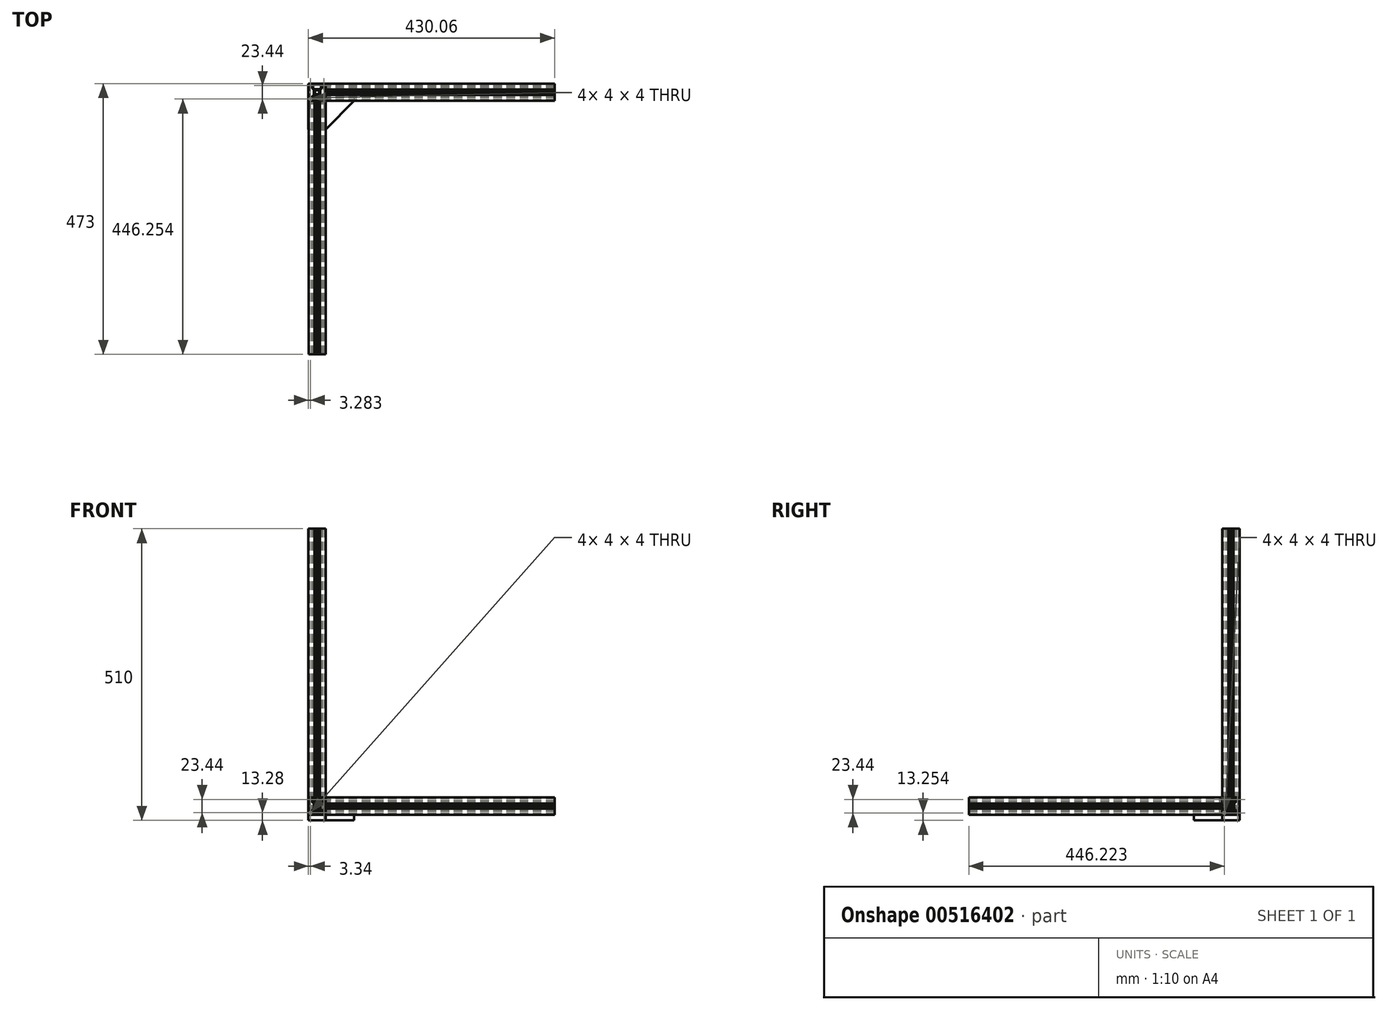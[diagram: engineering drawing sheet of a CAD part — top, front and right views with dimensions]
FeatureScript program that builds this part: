
annotation { "Feature Type Name" : "Feature", "Feature Type Description" : "" }
export const myFeature = defineFeature(function(context is Context, id is Id, definition is map)
    precondition{}
    {
        {
            var Q0;
            Q0=qCreatedBy(makeId("Front.planeOp"),FACE);
            var sketch = newSketch(context, id + "F0", { "sketchPlane" : qUnion([Q0])});
            skLineSegment(sketch, "E0", {"start": v(-15, 15) * mm, "end": v(-4.6, 15) * mm});
            skLineSegment(sketch, "E1", {"start": v(-4.6, 15) * mm, "end": v(-4.6, 14.5) * mm});
            skLineSegment(sketch, "E2", {"start": v(-4.6, 14.5) * mm, "end": v(-4.1, 14.5) * mm});
            skLineSegment(sketch, "E3", {"start": v(-4.1, 14.5) * mm, "end": v(-4.1, 12.8) * mm});
            skLineSegment(sketch, "E4", {"start": v(-4.1, 12.8) * mm, "end": v(-8.4, 12.8) * mm});
            skLineSegment(sketch, "E5", {"start": v(-8.4, 12.8) * mm, "end": v(-8.4, 9.8) * mm});
            skLineSegment(sketch, "E6", {"start": v(-8.4, 9.8) * mm, "end": v(-4.35, 5.75) * mm});
            skLineSegment(sketch, "E7", {"start": v(-4.35, 5.75) * mm, "end": v(-0.5, 5.75) * mm});
            skLineSegment(sketch, "E8", {"start": v(-0.5, 5.75) * mm, "end": v(0, 5.25) * mm});
            skLineSegment(sketch, "E9", {"start": v(0, 5.25) * mm, "end": v(0.5, 5.75) * mm});
            skLineSegment(sketch, "E10", {"start": v(0.5, 5.75) * mm, "end": v(4.35, 5.75) * mm});
            skLineSegment(sketch, "E11", {"start": v(4.35, 5.75) * mm, "end": v(8.4, 9.8) * mm});
            skLineSegment(sketch, "E12", {"start": v(8.4, 9.8) * mm, "end": v(8.4, 12.8) * mm});
            skLineSegment(sketch, "E13", {"start": v(8.4, 12.8) * mm, "end": v(4.6, 12.8) * mm});
            skLineSegment(sketch, "E14", {"start": v(4.6, 12.8) * mm, "end": v(4.6, 14.5) * mm});
            skLineSegment(sketch, "E15", {"start": v(4.6, 14.5) * mm, "end": v(5.1, 14.5) * mm});
            skLineSegment(sketch, "E16", {"start": v(5.1, 14.5) * mm, "end": v(5.1, 15) * mm});
            skLineSegment(sketch, "E17", {"start": v(5.1, 15) * mm, "end": v(15, 15) * mm});
            skLineSegment(sketch, "E18", {"start": v(15, 15) * mm, "end": v(15, 4.6) * mm});
            skLineSegment(sketch, "E19", {"start": v(15, 4.6) * mm, "end": v(14.5, 4.6) * mm});
            skLineSegment(sketch, "E20", {"start": v(14.5, 4.6) * mm, "end": v(14.5, 4.1) * mm});
            skLineSegment(sketch, "E21", {"start": v(14.5, 4.1) * mm, "end": v(12.8, 4.1) * mm});
            skLineSegment(sketch, "E22", {"start": v(12.8, 4.1) * mm, "end": v(12.8, 8.4) * mm});
            skLineSegment(sketch, "E23", {"start": v(12.8, 8.4) * mm, "end": v(9.8, 8.4) * mm});
            skLineSegment(sketch, "E24", {"start": v(9.8, 8.4) * mm, "end": v(5.75, 4.35) * mm});
            skLineSegment(sketch, "E25", {"start": v(5.75, 4.35) * mm, "end": v(5.75, 0.5) * mm});
            skLineSegment(sketch, "E26", {"start": v(5.25, 0) * mm, "end": v(5.75, 0.5) * mm});
            skLineSegment(sketch, "E27", {"start": v(5.75, -0.5) * mm, "end": v(5.25, 0) * mm});
            skLineSegment(sketch, "E28", {"start": v(5.75, -0.5) * mm, "end": v(5.75, -4.35) * mm});
            skLineSegment(sketch, "E29", {"start": v(5.75, -4.35) * mm, "end": v(9.8, -8.4) * mm});
            skLineSegment(sketch, "E30", {"start": v(9.8, -8.4) * mm, "end": v(12.8, -8.4) * mm});
            skLineSegment(sketch, "E31", {"start": v(12.8, -8.4) * mm, "end": v(12.8, -3.79) * mm});
            skLineSegment(sketch, "E32", {"start": v(12.8, -3.79) * mm, "end": v(14.5, -3.79) * mm});
            skLineSegment(sketch, "E33", {"start": v(14.5, -3.79) * mm, "end": v(14.5, -4.29) * mm});
            skLineSegment(sketch, "E34", {"start": v(14.5, -4.29) * mm, "end": v(15, -4.29) * mm});
            skLineSegment(sketch, "E35", {"start": v(15, -4.29) * mm, "end": v(15, -15) * mm});
            skLineSegment(sketch, "E36", {"start": v(15, -15) * mm, "end": v(5.1, -15) * mm});
            skLineSegment(sketch, "E37", {"start": v(5.1, -15) * mm, "end": v(5.1, -14.5) * mm});
            skLineSegment(sketch, "E38", {"start": v(5.1, -14.5) * mm, "end": v(4.6, -14.5) * mm});
            skLineSegment(sketch, "E39", {"start": v(4.6, -14.5) * mm, "end": v(4.6, -12.8) * mm});
            skLineSegment(sketch, "E40", {"start": v(4.6, -12.8) * mm, "end": v(8.4, -12.8) * mm});
            skLineSegment(sketch, "E41", {"start": v(8.4, -12.8) * mm, "end": v(8.4, -9.8) * mm});
            skLineSegment(sketch, "E42", {"start": v(8.4, -9.8) * mm, "end": v(4.35, -5.75) * mm});
            skLineSegment(sketch, "E43", {"start": v(4.35, -5.75) * mm, "end": v(0.5, -5.75) * mm});
            skLineSegment(sketch, "E44", {"start": v(0.5, -5.75) * mm, "end": v(0, -5.25) * mm});
            skLineSegment(sketch, "E45", {"start": v(0, -5.25) * mm, "end": v(-0.5, -5.75) * mm});
            skLineSegment(sketch, "E46", {"start": v(-0.5, -5.75) * mm, "end": v(-4.35, -5.75) * mm});
            skLineSegment(sketch, "E47", {"start": v(-4.35, -5.75) * mm, "end": v(-8.4, -9.8) * mm});
            skLineSegment(sketch, "E48", {"start": v(-8.4, -9.8) * mm, "end": v(-8.4, -12.8) * mm});
            skLineSegment(sketch, "E49", {"start": v(-8.4, -12.8) * mm, "end": v(-4.09, -12.8) * mm});
            skLineSegment(sketch, "E50", {"start": v(-4.09, -12.8) * mm, "end": v(-4.09, -14.5) * mm});
            skLineSegment(sketch, "E51", {"start": v(-4.09, -14.5) * mm, "end": v(-4.6, -14.5) * mm});
            skLineSegment(sketch, "E52", {"start": v(-4.6, -14.5) * mm, "end": v(-4.6, -15) * mm});
            skLineSegment(sketch, "E53", {"start": v(-4.6, -15) * mm, "end": v(-15, -15) * mm});
            skLineSegment(sketch, "E54", {"start": v(-15, -15) * mm, "end": v(-15, -4.29) * mm});
            skLineSegment(sketch, "E55", {"start": v(-15, -4.29) * mm, "end": v(-14.5, -4.29) * mm});
            skLineSegment(sketch, "E56", {"start": v(-14.5, -4.29) * mm, "end": v(-14.5, -4.1) * mm});
            skLineSegment(sketch, "E57", {"start": v(-14.5, -4.1) * mm, "end": v(-12.8, -4.1) * mm});
            skLineSegment(sketch, "E58", {"start": v(-12.8, -4.1) * mm, "end": v(-12.8, -8.4) * mm});
            skLineSegment(sketch, "E59", {"start": v(-12.8, -8.4) * mm, "end": v(-9.8, -8.4) * mm});
            skLineSegment(sketch, "E60", {"start": v(-9.8, -8.4) * mm, "end": v(-5.75, -4.35) * mm});
            skLineSegment(sketch, "E61", {"start": v(-5.75, -4.35) * mm, "end": v(-5.75, -0.5) * mm});
            skLineSegment(sketch, "E62", {"start": v(-5.75, -0.5) * mm, "end": v(-5.25, 0) * mm});
            skLineSegment(sketch, "E63", {"start": v(-5.25, 0) * mm, "end": v(-5.75, 0.5) * mm});
            skLineSegment(sketch, "E64", {"start": v(-5.75, 0.5) * mm, "end": v(-5.75, 4.35) * mm});
            skLineSegment(sketch, "E65", {"start": v(-5.75, 4.35) * mm, "end": v(-9.8, 8.4) * mm});
            skLineSegment(sketch, "E66", {"start": v(-9.8, 8.4) * mm, "end": v(-12.8, 8.4) * mm});
            skLineSegment(sketch, "E67", {"start": v(-12.8, 8.4) * mm, "end": v(-12.8, 4.1) * mm});
            skLineSegment(sketch, "E68", {"start": v(-12.8, 4.1) * mm, "end": v(-14.5, 4.1) * mm});
            skLineSegment(sketch, "E69", {"start": v(-14.5, 4.1) * mm, "end": v(-14.5, 4.6) * mm});
            skLineSegment(sketch, "E70", {"start": v(-14.5, 4.6) * mm, "end": v(-15, 4.6) * mm});
            skLineSegment(sketch, "E71", {"start": v(-15, 4.6) * mm, "end": v(-15, 15) * mm});
            skSolve(sketch);
        }
        {
            var Q0;
            Q0=qCreatedBy(makeId("Front.planeOp"),FACE);
            var sketch = newSketch(context, id + "F1", { "sketchPlane" : qUnion([Q0])});
            skCircle(sketch, "E72", {"center": v(0, 0) * mm, "radius": 3.7 * mm});
            skLineSegment(sketch, "E73.bottom", {"start": v(9.72, 13.72) * mm, "end": v(13.72, 13.72) * mm});
            skLineSegment(sketch, "E73.top", {"start": v(9.72, 9.72) * mm, "end": v(13.72, 9.72) * mm});
            skLineSegment(sketch, "E73.left", {"start": v(9.72, 13.72) * mm, "end": v(9.72, 9.72) * mm});
            skLineSegment(sketch, "E73.right", {"start": v(13.72, 13.72) * mm, "end": v(13.72, 9.72) * mm});
            skLineSegment(sketch, "E74.bottom", {"start": v(9.72, -9.72) * mm, "end": v(13.72, -9.72) * mm});
            skLineSegment(sketch, "E74.top", {"start": v(9.72, -13.72) * mm, "end": v(13.72, -13.72) * mm});
            skLineSegment(sketch, "E74.left", {"start": v(9.72, -9.72) * mm, "end": v(9.72, -13.72) * mm});
            skLineSegment(sketch, "E74.right", {"start": v(13.72, -9.72) * mm, "end": v(13.72, -13.72) * mm});
            skLineSegment(sketch, "E75.bottom", {"start": v(-13.72, -9.72) * mm, "end": v(-9.72, -9.72) * mm});
            skLineSegment(sketch, "E75.top", {"start": v(-13.72, -13.72) * mm, "end": v(-9.72, -13.72) * mm});
            skLineSegment(sketch, "E75.left", {"start": v(-13.72, -9.72) * mm, "end": v(-13.72, -13.72) * mm});
            skLineSegment(sketch, "E75.right", {"start": v(-9.72, -9.72) * mm, "end": v(-9.72, -13.72) * mm});
            skLineSegment(sketch, "E76.bottom", {"start": v(-13.72, 13.72) * mm, "end": v(-9.72, 13.72) * mm});
            skLineSegment(sketch, "E76.top", {"start": v(-13.72, 9.72) * mm, "end": v(-9.72, 9.72) * mm});
            skLineSegment(sketch, "E76.left", {"start": v(-13.72, 13.72) * mm, "end": v(-13.72, 9.72) * mm});
            skLineSegment(sketch, "E76.right", {"start": v(-9.72, 13.72) * mm, "end": v(-9.72, 9.72) * mm});
            skSolve(sketch);
        }
        {
            var Q0;
            Q0=qSketchRegion(id+"F0",true);
            extrude(context, id + "F2", {"entities" : qUnion([Q0]), "depth" : 443 * mm, "offsetDistance" : 25 * mm});
        }
        {
            var Q0;
            Q0=qSketchRegion(id+"F1",true);
            extrude(context, id + "F3", {"entities" : qUnion([Q0]), "operationType" : NewBodyOperationType.REMOVE, "endBound" : BoundingType.THROUGH_ALL, "depth" : 25 * mm, "offsetDistance" : 25 * mm});
        }
        {
            var Q0;
            Q0=qCreatedBy(makeId("Top.planeOp"),FACE);
            cPlane(context, id + "F4", {"entities" : qUnion([Q0]), "cplaneType" : CPlaneType.OFFSET, "offset" : 15 * mm, "width" : 150 * mm, "height" : 150 * mm});
        }
        {
            var Q0;
            Q0=qCreatedBy(id+"F4.planeOp",FACE);
            var sketch = newSketch(context, id + "F5", { "sketchPlane" : qUnion([Q0])});
            skLineSegment(sketch, "E77", {"start": v(-15.06, 14.97) * mm, "end": v(-4.66, 14.97) * mm});
            skLineSegment(sketch, "E78", {"start": v(-4.66, 14.97) * mm, "end": v(-4.66, 14.47) * mm});
            skLineSegment(sketch, "E79", {"start": v(-4.66, 14.47) * mm, "end": v(-4.16, 14.47) * mm});
            skLineSegment(sketch, "E80", {"start": v(-4.16, 14.47) * mm, "end": v(-4.16, 12.77) * mm});
            skLineSegment(sketch, "E81", {"start": v(-4.16, 12.77) * mm, "end": v(-8.46, 12.77) * mm});
            skLineSegment(sketch, "E82", {"start": v(-8.46, 12.77) * mm, "end": v(-8.46, 9.77) * mm});
            skLineSegment(sketch, "E83", {"start": v(-8.46, 9.77) * mm, "end": v(-4.4, 5.72) * mm});
            skLineSegment(sketch, "E84", {"start": v(-4.4, 5.72) * mm, "end": v(-0.56, 5.72) * mm});
            skLineSegment(sketch, "E85", {"start": v(-0.56, 5.72) * mm, "end": v(-0.06, 5.22) * mm});
            skLineSegment(sketch, "E86", {"start": v(-0.06, 5.22) * mm, "end": v(0.44, 5.72) * mm});
            skLineSegment(sketch, "E87", {"start": v(0.44, 5.72) * mm, "end": v(4.3, 5.72) * mm});
            skLineSegment(sketch, "E88", {"start": v(4.3, 5.72) * mm, "end": v(8.34, 9.77) * mm});
            skLineSegment(sketch, "E89", {"start": v(8.34, 9.77) * mm, "end": v(8.34, 12.77) * mm});
            skLineSegment(sketch, "E90", {"start": v(8.34, 12.77) * mm, "end": v(4.55, 12.77) * mm});
            skLineSegment(sketch, "E91", {"start": v(4.55, 12.77) * mm, "end": v(4.55, 14.47) * mm});
            skLineSegment(sketch, "E92", {"start": v(4.55, 14.47) * mm, "end": v(5.05, 14.47) * mm});
            skLineSegment(sketch, "E93", {"start": v(5.05, 14.47) * mm, "end": v(5.05, 14.97) * mm});
            skLineSegment(sketch, "E94", {"start": v(5.05, 14.97) * mm, "end": v(14.94, 14.97) * mm});
            skLineSegment(sketch, "E95", {"start": v(14.94, 14.97) * mm, "end": v(14.94, 4.57) * mm});
            skLineSegment(sketch, "E96", {"start": v(14.94, 4.57) * mm, "end": v(14.44, 4.57) * mm});
            skLineSegment(sketch, "E97", {"start": v(14.44, 4.57) * mm, "end": v(14.44, 4.07) * mm});
            skLineSegment(sketch, "E98", {"start": v(14.44, 4.07) * mm, "end": v(12.74, 4.07) * mm});
            skLineSegment(sketch, "E99", {"start": v(12.74, 4.07) * mm, "end": v(12.74, 8.37) * mm});
            skLineSegment(sketch, "E100", {"start": v(12.74, 8.37) * mm, "end": v(9.74, 8.37) * mm});
            skLineSegment(sketch, "E101", {"start": v(9.74, 8.37) * mm, "end": v(5.7, 4.32) * mm});
            skLineSegment(sketch, "E102", {"start": v(5.7, 4.32) * mm, "end": v(5.7, 0.47) * mm});
            skLineSegment(sketch, "E103", {"start": v(5.2, -0.03) * mm, "end": v(5.7, 0.47) * mm});
            skLineSegment(sketch, "E104", {"start": v(5.7, -0.53) * mm, "end": v(5.2, -0.03) * mm});
            skLineSegment(sketch, "E105", {"start": v(5.7, -0.53) * mm, "end": v(5.7, -4.38) * mm});
            skLineSegment(sketch, "E106", {"start": v(5.7, -4.38) * mm, "end": v(9.74, -8.43) * mm});
            skLineSegment(sketch, "E107", {"start": v(9.74, -8.43) * mm, "end": v(12.74, -8.43) * mm});
            skLineSegment(sketch, "E108", {"start": v(12.74, -8.43) * mm, "end": v(12.74, -3.81) * mm});
            skLineSegment(sketch, "E109", {"start": v(12.74, -3.81) * mm, "end": v(14.44, -3.81) * mm});
            skLineSegment(sketch, "E110", {"start": v(14.44, -3.81) * mm, "end": v(14.44, -4.31) * mm});
            skLineSegment(sketch, "E111", {"start": v(14.44, -4.31) * mm, "end": v(14.94, -4.31) * mm});
            skLineSegment(sketch, "E112", {"start": v(14.94, -4.31) * mm, "end": v(14.94, -15.03) * mm});
            skLineSegment(sketch, "E113", {"start": v(14.94, -15.03) * mm, "end": v(5.05, -15.03) * mm});
            skLineSegment(sketch, "E114", {"start": v(5.05, -15.03) * mm, "end": v(5.05, -14.53) * mm});
            skLineSegment(sketch, "E115", {"start": v(5.05, -14.53) * mm, "end": v(4.55, -14.53) * mm});
            skLineSegment(sketch, "E116", {"start": v(4.55, -14.53) * mm, "end": v(4.55, -12.83) * mm});
            skLineSegment(sketch, "E117", {"start": v(4.55, -12.83) * mm, "end": v(8.34, -12.83) * mm});
            skLineSegment(sketch, "E118", {"start": v(8.34, -12.83) * mm, "end": v(8.34, -9.83) * mm});
            skLineSegment(sketch, "E119", {"start": v(8.34, -9.83) * mm, "end": v(4.3, -5.78) * mm});
            skLineSegment(sketch, "E120", {"start": v(4.3, -5.78) * mm, "end": v(0.44, -5.78) * mm});
            skLineSegment(sketch, "E121", {"start": v(0.44, -5.78) * mm, "end": v(-0.06, -5.28) * mm});
            skLineSegment(sketch, "E122", {"start": v(-0.06, -5.28) * mm, "end": v(-0.56, -5.78) * mm});
            skLineSegment(sketch, "E123", {"start": v(-0.56, -5.78) * mm, "end": v(-4.4, -5.78) * mm});
            skLineSegment(sketch, "E124", {"start": v(-4.4, -5.78) * mm, "end": v(-8.46, -9.83) * mm});
            skLineSegment(sketch, "E125", {"start": v(-8.46, -9.83) * mm, "end": v(-8.46, -12.83) * mm});
            skLineSegment(sketch, "E126", {"start": v(-8.46, -12.83) * mm, "end": v(-4.14, -12.83) * mm});
            skLineSegment(sketch, "E127", {"start": v(-4.14, -12.83) * mm, "end": v(-4.14, -14.53) * mm});
            skLineSegment(sketch, "E128", {"start": v(-4.14, -14.53) * mm, "end": v(-4.66, -14.53) * mm});
            skLineSegment(sketch, "E129", {"start": v(-4.66, -14.53) * mm, "end": v(-4.66, -15.03) * mm});
            skLineSegment(sketch, "E130", {"start": v(-4.66, -15.03) * mm, "end": v(-15.06, -15.03) * mm});
            skLineSegment(sketch, "E131", {"start": v(-15.06, -15.03) * mm, "end": v(-15.06, -4.31) * mm});
            skLineSegment(sketch, "E132", {"start": v(-15.06, -4.31) * mm, "end": v(-14.56, -4.31) * mm});
            skLineSegment(sketch, "E133", {"start": v(-14.56, -4.31) * mm, "end": v(-14.56, -4.13) * mm});
            skLineSegment(sketch, "E134", {"start": v(-14.56, -4.13) * mm, "end": v(-12.86, -4.13) * mm});
            skLineSegment(sketch, "E135", {"start": v(-12.86, -4.13) * mm, "end": v(-12.86, -8.43) * mm});
            skLineSegment(sketch, "E136", {"start": v(-12.86, -8.43) * mm, "end": v(-9.86, -8.43) * mm});
            skLineSegment(sketch, "E137", {"start": v(-9.86, -8.43) * mm, "end": v(-5.8, -4.38) * mm});
            skLineSegment(sketch, "E138", {"start": v(-5.8, -4.38) * mm, "end": v(-5.8, -0.53) * mm});
            skLineSegment(sketch, "E139", {"start": v(-5.8, -0.53) * mm, "end": v(-5.3, -0.03) * mm});
            skLineSegment(sketch, "E140", {"start": v(-5.3, -0.03) * mm, "end": v(-5.8, 0.47) * mm});
            skLineSegment(sketch, "E141", {"start": v(-5.8, 0.47) * mm, "end": v(-5.8, 4.32) * mm});
            skLineSegment(sketch, "E142", {"start": v(-5.8, 4.32) * mm, "end": v(-9.86, 8.37) * mm});
            skLineSegment(sketch, "E143", {"start": v(-9.86, 8.37) * mm, "end": v(-12.86, 8.37) * mm});
            skLineSegment(sketch, "E144", {"start": v(-12.86, 8.37) * mm, "end": v(-12.86, 4.07) * mm});
            skLineSegment(sketch, "E145", {"start": v(-12.86, 4.07) * mm, "end": v(-14.56, 4.07) * mm});
            skLineSegment(sketch, "E146", {"start": v(-14.56, 4.07) * mm, "end": v(-14.56, 4.57) * mm});
            skLineSegment(sketch, "E147", {"start": v(-14.56, 4.57) * mm, "end": v(-15.06, 4.57) * mm});
            skLineSegment(sketch, "E148", {"start": v(-15.06, 4.57) * mm, "end": v(-15.06, 14.97) * mm});
            skSolve(sketch);
        }
        {
            var Q0;
            Q0=qCreatedBy(id+"F4.planeOp",FACE);
            var sketch = newSketch(context, id + "F6", { "sketchPlane" : qUnion([Q0])});
            skCircle(sketch, "E149", {"center": v(0, 0) * mm, "radius": 3.7 * mm});
            skLineSegment(sketch, "E150.bottom", {"start": v(9.66, 13.69) * mm, "end": v(13.66, 13.69) * mm});
            skLineSegment(sketch, "E150.top", {"start": v(9.66, 9.69) * mm, "end": v(13.66, 9.69) * mm});
            skLineSegment(sketch, "E150.left", {"start": v(9.66, 13.69) * mm, "end": v(9.66, 9.69) * mm});
            skLineSegment(sketch, "E150.right", {"start": v(13.66, 13.69) * mm, "end": v(13.66, 9.69) * mm});
            skLineSegment(sketch, "E151.bottom", {"start": v(9.66, -9.75) * mm, "end": v(13.66, -9.75) * mm});
            skLineSegment(sketch, "E151.top", {"start": v(9.66, -13.75) * mm, "end": v(13.66, -13.75) * mm});
            skLineSegment(sketch, "E151.left", {"start": v(9.66, -9.75) * mm, "end": v(9.66, -13.75) * mm});
            skLineSegment(sketch, "E151.right", {"start": v(13.66, -9.75) * mm, "end": v(13.66, -13.75) * mm});
            skLineSegment(sketch, "E152.bottom", {"start": v(-13.78, -9.75) * mm, "end": v(-9.78, -9.75) * mm});
            skLineSegment(sketch, "E152.top", {"start": v(-13.78, -13.75) * mm, "end": v(-9.78, -13.75) * mm});
            skLineSegment(sketch, "E152.left", {"start": v(-13.78, -9.75) * mm, "end": v(-13.78, -13.75) * mm});
            skLineSegment(sketch, "E152.right", {"start": v(-9.78, -9.75) * mm, "end": v(-9.78, -13.75) * mm});
            skLineSegment(sketch, "E153.bottom", {"start": v(-13.78, 13.7) * mm, "end": v(-9.78, 13.7) * mm});
            skLineSegment(sketch, "E153.top", {"start": v(-13.78, 9.7) * mm, "end": v(-9.78, 9.7) * mm});
            skLineSegment(sketch, "E153.left", {"start": v(-13.78, 13.7) * mm, "end": v(-13.78, 9.7) * mm});
            skLineSegment(sketch, "E153.right", {"start": v(-9.78, 13.7) * mm, "end": v(-9.78, 9.7) * mm});
            skSolve(sketch);
        }
        {
            var Q0;
            Q0 = qSketchRegion(id + "F5", true);
            extrude(context, id + "F7", {"entities" : qUnion([Q0]), "depth" : 500 * mm, "offsetDistance" : 25 * mm});
        }
        {
            var Q0;
            Q0 = qSketchRegion(id + "F6", true);
            extrude(context, id + "F8", {"entities" : qUnion([Q0]), "operationType" : NewBodyOperationType.REMOVE, "endBound" : BoundingType.THROUGH_ALL, "depth" : 25 * mm, "offsetDistance" : 25 * mm});
        }
        {
            var Q0;
            Q0=makeQuery(id+"F7.opExtrude","SWEPT_BODY",BODY,{"disambiguationData":[OSD([sQuery(id+"F5.wireOp",EDGE,"E77"),sQuery(id+"F5.wireOp",EDGE,"E78"),sQuery(id+"F5.wireOp",EDGE,"E79"),sQuery(id+"F5.wireOp",EDGE,"E80"),sQuery(id+"F5.wireOp",EDGE,"E81"),sQuery(id+"F5.wireOp",EDGE,"E82"),sQuery(id+"F5.wireOp",EDGE,"E83"),sQuery(id+"F5.wireOp",EDGE,"E84"),sQuery(id+"F5.wireOp",EDGE,"E85"),sQuery(id+"F5.wireOp",EDGE,"E86"),sQuery(id+"F5.wireOp",EDGE,"E87"),sQuery(id+"F5.wireOp",EDGE,"E88"),sQuery(id+"F5.wireOp",EDGE,"E89"),sQuery(id+"F5.wireOp",EDGE,"E90"),sQuery(id+"F5.wireOp",EDGE,"E91"),sQuery(id+"F5.wireOp",EDGE,"E92"),sQuery(id+"F5.wireOp",EDGE,"E93"),sQuery(id+"F5.wireOp",EDGE,"E94"),sQuery(id+"F5.wireOp",EDGE,"E95"),sQuery(id+"F5.wireOp",EDGE,"E96"),sQuery(id+"F5.wireOp",EDGE,"E97"),sQuery(id+"F5.wireOp",EDGE,"E98"),sQuery(id+"F5.wireOp",EDGE,"E99"),sQuery(id+"F5.wireOp",EDGE,"E100"),sQuery(id+"F5.wireOp",EDGE,"E101"),sQuery(id+"F5.wireOp",EDGE,"E102"),sQuery(id+"F5.wireOp",EDGE,"E103"),sQuery(id+"F5.wireOp",EDGE,"E104"),sQuery(id+"F5.wireOp",EDGE,"E105"),sQuery(id+"F5.wireOp",EDGE,"E106"),sQuery(id+"F5.wireOp",EDGE,"E107"),sQuery(id+"F5.wireOp",EDGE,"E108"),sQuery(id+"F5.wireOp",EDGE,"E109"),sQuery(id+"F5.wireOp",EDGE,"E110"),sQuery(id+"F5.wireOp",EDGE,"E111"),sQuery(id+"F5.wireOp",EDGE,"E112"),sQuery(id+"F5.wireOp",EDGE,"E113"),sQuery(id+"F5.wireOp",EDGE,"E114"),sQuery(id+"F5.wireOp",EDGE,"E115"),sQuery(id+"F5.wireOp",EDGE,"E116"),sQuery(id+"F5.wireOp",EDGE,"E117"),sQuery(id+"F5.wireOp",EDGE,"E118"),sQuery(id+"F5.wireOp",EDGE,"E119"),sQuery(id+"F5.wireOp",EDGE,"E120"),sQuery(id+"F5.wireOp",EDGE,"E121"),sQuery(id+"F5.wireOp",EDGE,"E122"),sQuery(id+"F5.wireOp",EDGE,"E123"),sQuery(id+"F5.wireOp",EDGE,"E124"),sQuery(id+"F5.wireOp",EDGE,"E125"),sQuery(id+"F5.wireOp",EDGE,"E126"),sQuery(id+"F5.wireOp",EDGE,"E127"),sQuery(id+"F5.wireOp",EDGE,"E128"),sQuery(id+"F5.wireOp",EDGE,"E129"),sQuery(id+"F5.wireOp",EDGE,"E130"),sQuery(id+"F5.wireOp",EDGE,"E131"),sQuery(id+"F5.wireOp",EDGE,"E132"),sQuery(id+"F5.wireOp",EDGE,"E133"),sQuery(id+"F5.wireOp",EDGE,"E134"),sQuery(id+"F5.wireOp",EDGE,"E135"),sQuery(id+"F5.wireOp",EDGE,"E136"),sQuery(id+"F5.wireOp",EDGE,"E137"),sQuery(id+"F5.wireOp",EDGE,"E138"),sQuery(id+"F5.wireOp",EDGE,"E139"),sQuery(id+"F5.wireOp",EDGE,"E140"),sQuery(id+"F5.wireOp",EDGE,"E141"),sQuery(id+"F5.wireOp",EDGE,"E142"),sQuery(id+"F5.wireOp",EDGE,"E143"),sQuery(id+"F5.wireOp",EDGE,"E144"),sQuery(id+"F5.wireOp",EDGE,"E145"),sQuery(id+"F5.wireOp",EDGE,"E146"),sQuery(id+"F5.wireOp",EDGE,"E147"),sQuery(id+"F5.wireOp",EDGE,"E148")])]});
            transform(context, id + "F9", {"entities" : qUnion([Q0]), "transformType" : TransformType.TRANSLATION_3D, "dx" : 0 * mm, "dy" : 15 * mm, "dz" : 0 * mm, "makeCopy" : false});
        }
        {
            var Q0;
            Q0=makeQuery(id+"F7.opExtrude","SWEPT_BODY",BODY,{"disambiguationData":[OSD([sQuery(id+"F5.wireOp",EDGE,"E77"),sQuery(id+"F5.wireOp",EDGE,"E78"),sQuery(id+"F5.wireOp",EDGE,"E79"),sQuery(id+"F5.wireOp",EDGE,"E80"),sQuery(id+"F5.wireOp",EDGE,"E81"),sQuery(id+"F5.wireOp",EDGE,"E82"),sQuery(id+"F5.wireOp",EDGE,"E83"),sQuery(id+"F5.wireOp",EDGE,"E84"),sQuery(id+"F5.wireOp",EDGE,"E85"),sQuery(id+"F5.wireOp",EDGE,"E86"),sQuery(id+"F5.wireOp",EDGE,"E87"),sQuery(id+"F5.wireOp",EDGE,"E88"),sQuery(id+"F5.wireOp",EDGE,"E89"),sQuery(id+"F5.wireOp",EDGE,"E90"),sQuery(id+"F5.wireOp",EDGE,"E91"),sQuery(id+"F5.wireOp",EDGE,"E92"),sQuery(id+"F5.wireOp",EDGE,"E93"),sQuery(id+"F5.wireOp",EDGE,"E94"),sQuery(id+"F5.wireOp",EDGE,"E95"),sQuery(id+"F5.wireOp",EDGE,"E96"),sQuery(id+"F5.wireOp",EDGE,"E97"),sQuery(id+"F5.wireOp",EDGE,"E98"),sQuery(id+"F5.wireOp",EDGE,"E99"),sQuery(id+"F5.wireOp",EDGE,"E100"),sQuery(id+"F5.wireOp",EDGE,"E101"),sQuery(id+"F5.wireOp",EDGE,"E102"),sQuery(id+"F5.wireOp",EDGE,"E103"),sQuery(id+"F5.wireOp",EDGE,"E104"),sQuery(id+"F5.wireOp",EDGE,"E105"),sQuery(id+"F5.wireOp",EDGE,"E106"),sQuery(id+"F5.wireOp",EDGE,"E107"),sQuery(id+"F5.wireOp",EDGE,"E108"),sQuery(id+"F5.wireOp",EDGE,"E109"),sQuery(id+"F5.wireOp",EDGE,"E110"),sQuery(id+"F5.wireOp",EDGE,"E111"),sQuery(id+"F5.wireOp",EDGE,"E112"),sQuery(id+"F5.wireOp",EDGE,"E113"),sQuery(id+"F5.wireOp",EDGE,"E114"),sQuery(id+"F5.wireOp",EDGE,"E115"),sQuery(id+"F5.wireOp",EDGE,"E116"),sQuery(id+"F5.wireOp",EDGE,"E117"),sQuery(id+"F5.wireOp",EDGE,"E118"),sQuery(id+"F5.wireOp",EDGE,"E119"),sQuery(id+"F5.wireOp",EDGE,"E120"),sQuery(id+"F5.wireOp",EDGE,"E121"),sQuery(id+"F5.wireOp",EDGE,"E122"),sQuery(id+"F5.wireOp",EDGE,"E123"),sQuery(id+"F5.wireOp",EDGE,"E124"),sQuery(id+"F5.wireOp",EDGE,"E125"),sQuery(id+"F5.wireOp",EDGE,"E126"),sQuery(id+"F5.wireOp",EDGE,"E127"),sQuery(id+"F5.wireOp",EDGE,"E128"),sQuery(id+"F5.wireOp",EDGE,"E129"),sQuery(id+"F5.wireOp",EDGE,"E130"),sQuery(id+"F5.wireOp",EDGE,"E131"),sQuery(id+"F5.wireOp",EDGE,"E132"),sQuery(id+"F5.wireOp",EDGE,"E133"),sQuery(id+"F5.wireOp",EDGE,"E134"),sQuery(id+"F5.wireOp",EDGE,"E135"),sQuery(id+"F5.wireOp",EDGE,"E136"),sQuery(id+"F5.wireOp",EDGE,"E137"),sQuery(id+"F5.wireOp",EDGE,"E138"),sQuery(id+"F5.wireOp",EDGE,"E139"),sQuery(id+"F5.wireOp",EDGE,"E140"),sQuery(id+"F5.wireOp",EDGE,"E141"),sQuery(id+"F5.wireOp",EDGE,"E142"),sQuery(id+"F5.wireOp",EDGE,"E143"),sQuery(id+"F5.wireOp",EDGE,"E144"),sQuery(id+"F5.wireOp",EDGE,"E145"),sQuery(id+"F5.wireOp",EDGE,"E146"),sQuery(id+"F5.wireOp",EDGE,"E147"),sQuery(id+"F5.wireOp",EDGE,"E148")])]});
            transform(context, id + "F10", {"entities" : qUnion([Q0]), "transformType" : TransformType.TRANSLATION_3D, "dx" : 0 * mm, "dy" : 0 * mm, "dz" : -30 * mm, "makeCopy" : false});
        }
        {
            var Q0;
            Q0=qCreatedBy(makeId("Right.planeOp"),FACE);
            cPlane(context, id + "F11", {"entities" : qUnion([Q0]), "cplaneType" : CPlaneType.OFFSET, "offset" : 15 * mm, "width" : 150 * mm, "height" : 150 * mm});
        }
        {
            var Q0;
            Q0=qCreatedBy(id+"F11.planeOp",FACE);
            var sketch = newSketch(context, id + "F12", { "sketchPlane" : qUnion([Q0])});
            skLineSegment(sketch, "E154", {"start": v(-15.06, 14.97) * mm, "end": v(-4.66, 14.97) * mm});
            skLineSegment(sketch, "E155", {"start": v(-4.66, 14.97) * mm, "end": v(-4.66, 14.47) * mm});
            skLineSegment(sketch, "E156", {"start": v(-4.66, 14.47) * mm, "end": v(-4.16, 14.47) * mm});
            skLineSegment(sketch, "E157", {"start": v(-4.16, 14.47) * mm, "end": v(-4.16, 12.77) * mm});
            skLineSegment(sketch, "E158", {"start": v(-4.16, 12.77) * mm, "end": v(-8.46, 12.77) * mm});
            skLineSegment(sketch, "E159", {"start": v(-8.46, 12.77) * mm, "end": v(-8.46, 9.77) * mm});
            skLineSegment(sketch, "E160", {"start": v(-8.46, 9.77) * mm, "end": v(-4.4, 5.72) * mm});
            skLineSegment(sketch, "E161", {"start": v(-4.4, 5.72) * mm, "end": v(-0.56, 5.72) * mm});
            skLineSegment(sketch, "E162", {"start": v(-0.56, 5.72) * mm, "end": v(-0.06, 5.22) * mm});
            skLineSegment(sketch, "E163", {"start": v(-0.06, 5.22) * mm, "end": v(0.44, 5.72) * mm});
            skLineSegment(sketch, "E164", {"start": v(0.44, 5.72) * mm, "end": v(4.3, 5.72) * mm});
            skLineSegment(sketch, "E165", {"start": v(4.3, 5.72) * mm, "end": v(8.34, 9.77) * mm});
            skLineSegment(sketch, "E166", {"start": v(8.34, 9.77) * mm, "end": v(8.34, 12.77) * mm});
            skLineSegment(sketch, "E167", {"start": v(8.34, 12.77) * mm, "end": v(4.55, 12.77) * mm});
            skLineSegment(sketch, "E168", {"start": v(4.55, 12.77) * mm, "end": v(4.55, 14.47) * mm});
            skLineSegment(sketch, "E169", {"start": v(4.55, 14.47) * mm, "end": v(5.05, 14.47) * mm});
            skLineSegment(sketch, "E170", {"start": v(5.05, 14.47) * mm, "end": v(5.05, 14.97) * mm});
            skLineSegment(sketch, "E171", {"start": v(5.05, 14.97) * mm, "end": v(14.94, 14.97) * mm});
            skLineSegment(sketch, "E172", {"start": v(14.94, 14.97) * mm, "end": v(14.94, 4.57) * mm});
            skLineSegment(sketch, "E173", {"start": v(14.94, 4.57) * mm, "end": v(14.44, 4.57) * mm});
            skLineSegment(sketch, "E174", {"start": v(14.44, 4.57) * mm, "end": v(14.44, 4.07) * mm});
            skLineSegment(sketch, "E175", {"start": v(14.44, 4.07) * mm, "end": v(12.74, 4.07) * mm});
            skLineSegment(sketch, "E176", {"start": v(12.74, 4.07) * mm, "end": v(12.74, 8.37) * mm});
            skLineSegment(sketch, "E177", {"start": v(12.74, 8.37) * mm, "end": v(9.74, 8.37) * mm});
            skLineSegment(sketch, "E178", {"start": v(9.74, 8.37) * mm, "end": v(5.7, 4.32) * mm});
            skLineSegment(sketch, "E179", {"start": v(5.7, 4.32) * mm, "end": v(5.7, 0.47) * mm});
            skLineSegment(sketch, "E180", {"start": v(5.2, -0.03) * mm, "end": v(5.7, 0.47) * mm});
            skLineSegment(sketch, "E181", {"start": v(5.7, -0.53) * mm, "end": v(5.2, -0.03) * mm});
            skLineSegment(sketch, "E182", {"start": v(5.7, -0.53) * mm, "end": v(5.7, -4.38) * mm});
            skLineSegment(sketch, "E183", {"start": v(5.7, -4.38) * mm, "end": v(9.74, -8.43) * mm});
            skLineSegment(sketch, "E184", {"start": v(9.74, -8.43) * mm, "end": v(12.74, -8.43) * mm});
            skLineSegment(sketch, "E185", {"start": v(12.74, -8.43) * mm, "end": v(12.74, -3.81) * mm});
            skLineSegment(sketch, "E186", {"start": v(12.74, -3.81) * mm, "end": v(14.44, -3.81) * mm});
            skLineSegment(sketch, "E187", {"start": v(14.44, -3.81) * mm, "end": v(14.44, -4.31) * mm});
            skLineSegment(sketch, "E188", {"start": v(14.44, -4.31) * mm, "end": v(14.94, -4.31) * mm});
            skLineSegment(sketch, "E189", {"start": v(14.94, -4.31) * mm, "end": v(14.94, -15.03) * mm});
            skLineSegment(sketch, "E190", {"start": v(14.94, -15.03) * mm, "end": v(5.05, -15.03) * mm});
            skLineSegment(sketch, "E191", {"start": v(5.05, -15.03) * mm, "end": v(5.05, -14.53) * mm});
            skLineSegment(sketch, "E192", {"start": v(5.05, -14.53) * mm, "end": v(4.55, -14.53) * mm});
            skLineSegment(sketch, "E193", {"start": v(4.55, -14.53) * mm, "end": v(4.55, -12.83) * mm});
            skLineSegment(sketch, "E194", {"start": v(4.55, -12.83) * mm, "end": v(8.34, -12.83) * mm});
            skLineSegment(sketch, "E195", {"start": v(8.34, -12.83) * mm, "end": v(8.34, -9.83) * mm});
            skLineSegment(sketch, "E196", {"start": v(8.34, -9.83) * mm, "end": v(4.3, -5.78) * mm});
            skLineSegment(sketch, "E197", {"start": v(4.3, -5.78) * mm, "end": v(0.44, -5.78) * mm});
            skLineSegment(sketch, "E198", {"start": v(0.44, -5.78) * mm, "end": v(-0.06, -5.28) * mm});
            skLineSegment(sketch, "E199", {"start": v(-0.06, -5.28) * mm, "end": v(-0.56, -5.78) * mm});
            skLineSegment(sketch, "E200", {"start": v(-0.56, -5.78) * mm, "end": v(-4.4, -5.78) * mm});
            skLineSegment(sketch, "E201", {"start": v(-4.4, -5.78) * mm, "end": v(-8.46, -9.83) * mm});
            skLineSegment(sketch, "E202", {"start": v(-8.46, -9.83) * mm, "end": v(-8.46, -12.83) * mm});
            skLineSegment(sketch, "E203", {"start": v(-8.46, -12.83) * mm, "end": v(-4.14, -12.83) * mm});
            skLineSegment(sketch, "E204", {"start": v(-4.14, -12.83) * mm, "end": v(-4.14, -14.53) * mm});
            skLineSegment(sketch, "E205", {"start": v(-4.14, -14.53) * mm, "end": v(-4.66, -14.53) * mm});
            skLineSegment(sketch, "E206", {"start": v(-4.66, -14.53) * mm, "end": v(-4.66, -15.03) * mm});
            skLineSegment(sketch, "E207", {"start": v(-4.66, -15.03) * mm, "end": v(-15.06, -15.03) * mm});
            skLineSegment(sketch, "E208", {"start": v(-15.06, -15.03) * mm, "end": v(-15.06, -4.31) * mm});
            skLineSegment(sketch, "E209", {"start": v(-15.06, -4.31) * mm, "end": v(-14.56, -4.31) * mm});
            skLineSegment(sketch, "E210", {"start": v(-14.56, -4.31) * mm, "end": v(-14.56, -4.13) * mm});
            skLineSegment(sketch, "E211", {"start": v(-14.56, -4.13) * mm, "end": v(-12.86, -4.13) * mm});
            skLineSegment(sketch, "E212", {"start": v(-12.86, -4.13) * mm, "end": v(-12.86, -8.43) * mm});
            skLineSegment(sketch, "E213", {"start": v(-12.86, -8.43) * mm, "end": v(-9.86, -8.43) * mm});
            skLineSegment(sketch, "E214", {"start": v(-9.86, -8.43) * mm, "end": v(-5.8, -4.38) * mm});
            skLineSegment(sketch, "E215", {"start": v(-5.8, -4.38) * mm, "end": v(-5.8, -0.53) * mm});
            skLineSegment(sketch, "E216", {"start": v(-5.8, -0.53) * mm, "end": v(-5.3, -0.03) * mm});
            skLineSegment(sketch, "E217", {"start": v(-5.3, -0.03) * mm, "end": v(-5.8, 0.47) * mm});
            skLineSegment(sketch, "E218", {"start": v(-5.8, 0.47) * mm, "end": v(-5.8, 4.32) * mm});
            skLineSegment(sketch, "E219", {"start": v(-5.8, 4.32) * mm, "end": v(-9.86, 8.37) * mm});
            skLineSegment(sketch, "E220", {"start": v(-9.86, 8.37) * mm, "end": v(-12.86, 8.37) * mm});
            skLineSegment(sketch, "E221", {"start": v(-12.86, 8.37) * mm, "end": v(-12.86, 4.07) * mm});
            skLineSegment(sketch, "E222", {"start": v(-12.86, 4.07) * mm, "end": v(-14.56, 4.07) * mm});
            skLineSegment(sketch, "E223", {"start": v(-14.56, 4.07) * mm, "end": v(-14.56, 4.57) * mm});
            skLineSegment(sketch, "E224", {"start": v(-14.56, 4.57) * mm, "end": v(-15.06, 4.57) * mm});
            skLineSegment(sketch, "E225", {"start": v(-15.06, 4.57) * mm, "end": v(-15.06, 14.97) * mm});
            skSolve(sketch);
        }
        {
            var Q0;
            Q0=qCreatedBy(id+"F11.planeOp",FACE);
            var sketch = newSketch(context, id + "F13", { "sketchPlane" : qUnion([Q0])});
            skCircle(sketch, "E226", {"center": v(0, 0) * mm, "radius": 3.7 * mm});
            skLineSegment(sketch, "E227.bottom", {"start": v(9.66, 13.69) * mm, "end": v(13.66, 13.69) * mm});
            skLineSegment(sketch, "E227.top", {"start": v(9.66, 9.69) * mm, "end": v(13.66, 9.69) * mm});
            skLineSegment(sketch, "E227.left", {"start": v(9.66, 13.69) * mm, "end": v(9.66, 9.69) * mm});
            skLineSegment(sketch, "E227.right", {"start": v(13.66, 13.69) * mm, "end": v(13.66, 9.69) * mm});
            skLineSegment(sketch, "E228.bottom", {"start": v(9.66, -9.75) * mm, "end": v(13.66, -9.75) * mm});
            skLineSegment(sketch, "E228.top", {"start": v(9.66, -13.75) * mm, "end": v(13.66, -13.75) * mm});
            skLineSegment(sketch, "E228.left", {"start": v(9.66, -9.75) * mm, "end": v(9.66, -13.75) * mm});
            skLineSegment(sketch, "E228.right", {"start": v(13.66, -9.75) * mm, "end": v(13.66, -13.75) * mm});
            skLineSegment(sketch, "E229.bottom", {"start": v(-13.78, -9.75) * mm, "end": v(-9.78, -9.75) * mm});
            skLineSegment(sketch, "E229.top", {"start": v(-13.78, -13.75) * mm, "end": v(-9.78, -13.75) * mm});
            skLineSegment(sketch, "E229.left", {"start": v(-13.78, -9.75) * mm, "end": v(-13.78, -13.75) * mm});
            skLineSegment(sketch, "E229.right", {"start": v(-9.78, -9.75) * mm, "end": v(-9.78, -13.75) * mm});
            skLineSegment(sketch, "E230.bottom", {"start": v(-13.78, 13.7) * mm, "end": v(-9.78, 13.7) * mm});
            skLineSegment(sketch, "E230.top", {"start": v(-13.78, 9.7) * mm, "end": v(-9.78, 9.7) * mm});
            skLineSegment(sketch, "E230.left", {"start": v(-13.78, 13.7) * mm, "end": v(-13.78, 9.7) * mm});
            skLineSegment(sketch, "E230.right", {"start": v(-9.78, 13.7) * mm, "end": v(-9.78, 9.7) * mm});
            skSolve(sketch);
        }
        {
            var Q0;
            Q0 = qSketchRegion(id + "F12", true);
            extrude(context, id + "F14", {"entities" : qUnion([Q0]), "depth" : 400 * mm, "offsetDistance" : 25 * mm});
        }
        {
            var Q0;
            Q0 = qSketchRegion(id + "F13", true);
            extrude(context, id + "F15", {"entities" : qUnion([Q0]), "operationType" : NewBodyOperationType.REMOVE, "endBound" : BoundingType.THROUGH_ALL, "depth" : 25 * mm, "offsetDistance" : 25 * mm});
        }
        {
            var Q0;
            Q0=makeQuery(id+"F14.opExtrude","SWEPT_BODY",BODY,{"disambiguationData":[OSD([sQuery(id+"F12.wireOp",EDGE,"E154"),sQuery(id+"F12.wireOp",EDGE,"E155"),sQuery(id+"F12.wireOp",EDGE,"E156"),sQuery(id+"F12.wireOp",EDGE,"E157"),sQuery(id+"F12.wireOp",EDGE,"E158"),sQuery(id+"F12.wireOp",EDGE,"E159"),sQuery(id+"F12.wireOp",EDGE,"E160"),sQuery(id+"F12.wireOp",EDGE,"E161"),sQuery(id+"F12.wireOp",EDGE,"E162"),sQuery(id+"F12.wireOp",EDGE,"E163"),sQuery(id+"F12.wireOp",EDGE,"E164"),sQuery(id+"F12.wireOp",EDGE,"E165"),sQuery(id+"F12.wireOp",EDGE,"E166"),sQuery(id+"F12.wireOp",EDGE,"E167"),sQuery(id+"F12.wireOp",EDGE,"E168"),sQuery(id+"F12.wireOp",EDGE,"E169"),sQuery(id+"F12.wireOp",EDGE,"E170"),sQuery(id+"F12.wireOp",EDGE,"E171"),sQuery(id+"F12.wireOp",EDGE,"E172"),sQuery(id+"F12.wireOp",EDGE,"E173"),sQuery(id+"F12.wireOp",EDGE,"E174"),sQuery(id+"F12.wireOp",EDGE,"E175"),sQuery(id+"F12.wireOp",EDGE,"E176"),sQuery(id+"F12.wireOp",EDGE,"E177"),sQuery(id+"F12.wireOp",EDGE,"E178"),sQuery(id+"F12.wireOp",EDGE,"E179"),sQuery(id+"F12.wireOp",EDGE,"E180"),sQuery(id+"F12.wireOp",EDGE,"E181"),sQuery(id+"F12.wireOp",EDGE,"E182"),sQuery(id+"F12.wireOp",EDGE,"E183"),sQuery(id+"F12.wireOp",EDGE,"E184"),sQuery(id+"F12.wireOp",EDGE,"E185"),sQuery(id+"F12.wireOp",EDGE,"E186"),sQuery(id+"F12.wireOp",EDGE,"E187"),sQuery(id+"F12.wireOp",EDGE,"E188"),sQuery(id+"F12.wireOp",EDGE,"E189"),sQuery(id+"F12.wireOp",EDGE,"E190"),sQuery(id+"F12.wireOp",EDGE,"E191"),sQuery(id+"F12.wireOp",EDGE,"E192"),sQuery(id+"F12.wireOp",EDGE,"E193"),sQuery(id+"F12.wireOp",EDGE,"E194"),sQuery(id+"F12.wireOp",EDGE,"E195"),sQuery(id+"F12.wireOp",EDGE,"E196"),sQuery(id+"F12.wireOp",EDGE,"E197"),sQuery(id+"F12.wireOp",EDGE,"E198"),sQuery(id+"F12.wireOp",EDGE,"E199"),sQuery(id+"F12.wireOp",EDGE,"E200"),sQuery(id+"F12.wireOp",EDGE,"E201"),sQuery(id+"F12.wireOp",EDGE,"E202"),sQuery(id+"F12.wireOp",EDGE,"E203"),sQuery(id+"F12.wireOp",EDGE,"E204"),sQuery(id+"F12.wireOp",EDGE,"E205"),sQuery(id+"F12.wireOp",EDGE,"E206"),sQuery(id+"F12.wireOp",EDGE,"E207"),sQuery(id+"F12.wireOp",EDGE,"E208"),sQuery(id+"F12.wireOp",EDGE,"E209"),sQuery(id+"F12.wireOp",EDGE,"E210"),sQuery(id+"F12.wireOp",EDGE,"E211"),sQuery(id+"F12.wireOp",EDGE,"E212"),sQuery(id+"F12.wireOp",EDGE,"E213"),sQuery(id+"F12.wireOp",EDGE,"E214"),sQuery(id+"F12.wireOp",EDGE,"E215"),sQuery(id+"F12.wireOp",EDGE,"E216"),sQuery(id+"F12.wireOp",EDGE,"E217"),sQuery(id+"F12.wireOp",EDGE,"E218"),sQuery(id+"F12.wireOp",EDGE,"E219"),sQuery(id+"F12.wireOp",EDGE,"E220"),sQuery(id+"F12.wireOp",EDGE,"E221"),sQuery(id+"F12.wireOp",EDGE,"E222"),sQuery(id+"F12.wireOp",EDGE,"E223"),sQuery(id+"F12.wireOp",EDGE,"E224"),sQuery(id+"F12.wireOp",EDGE,"E225")])]});
            transform(context, id + "F16", {"entities" : qUnion([Q0]), "transformType" : TransformType.TRANSLATION_3D, "dx" : 0 * mm, "dy" : 15 * mm, "dz" : 0 * mm, "makeCopy" : false});
        }
        {
            var Q0;
            Q0=qCreatedBy(makeId("Top.planeOp"),FACE);
            cPlane(context, id + "F17", {"entities" : qUnion([Q0]), "cplaneType" : CPlaneType.OFFSET, "offset" : 25 * mm, "oppositeDirection" : true, "width" : 150 * mm, "height" : 150 * mm});
        }
        {
            var Q0;
            Q0=qCreatedBy(id+"F17.planeOp",FACE);
            var sketch = newSketch(context, id + "F18", { "sketchPlane" : qUnion([Q0])});
            skLineSegment(sketch, "E231", {"start": v(-15.06, -50.03) * mm, "end": v(-15.06, 29.97) * mm});
            skLineSegment(sketch, "E232", {"start": v(-15.06, 29.97) * mm, "end": v(64.94, 30) * mm});
            skLineSegment(sketch, "E233", {"start": v(64.94, 30) * mm, "end": v(64.95, 0) * mm});
            skLineSegment(sketch, "E234", {"start": v(64.95, 0) * mm, "end": v(14.94, -50.03) * mm});
            skLineSegment(sketch, "E235", {"start": v(14.94, -50.03) * mm, "end": v(-15.06, -50.03) * mm});
            skSolve(sketch);
        }
        {
            var Q0;
            Q0 = qSketchRegion(id + "F18", true);
            extrude(context, id + "F19", {"entities" : qUnion([Q0]), "depth" : 10 * mm, "offsetDistance" : 25 * mm});
        }
    });
